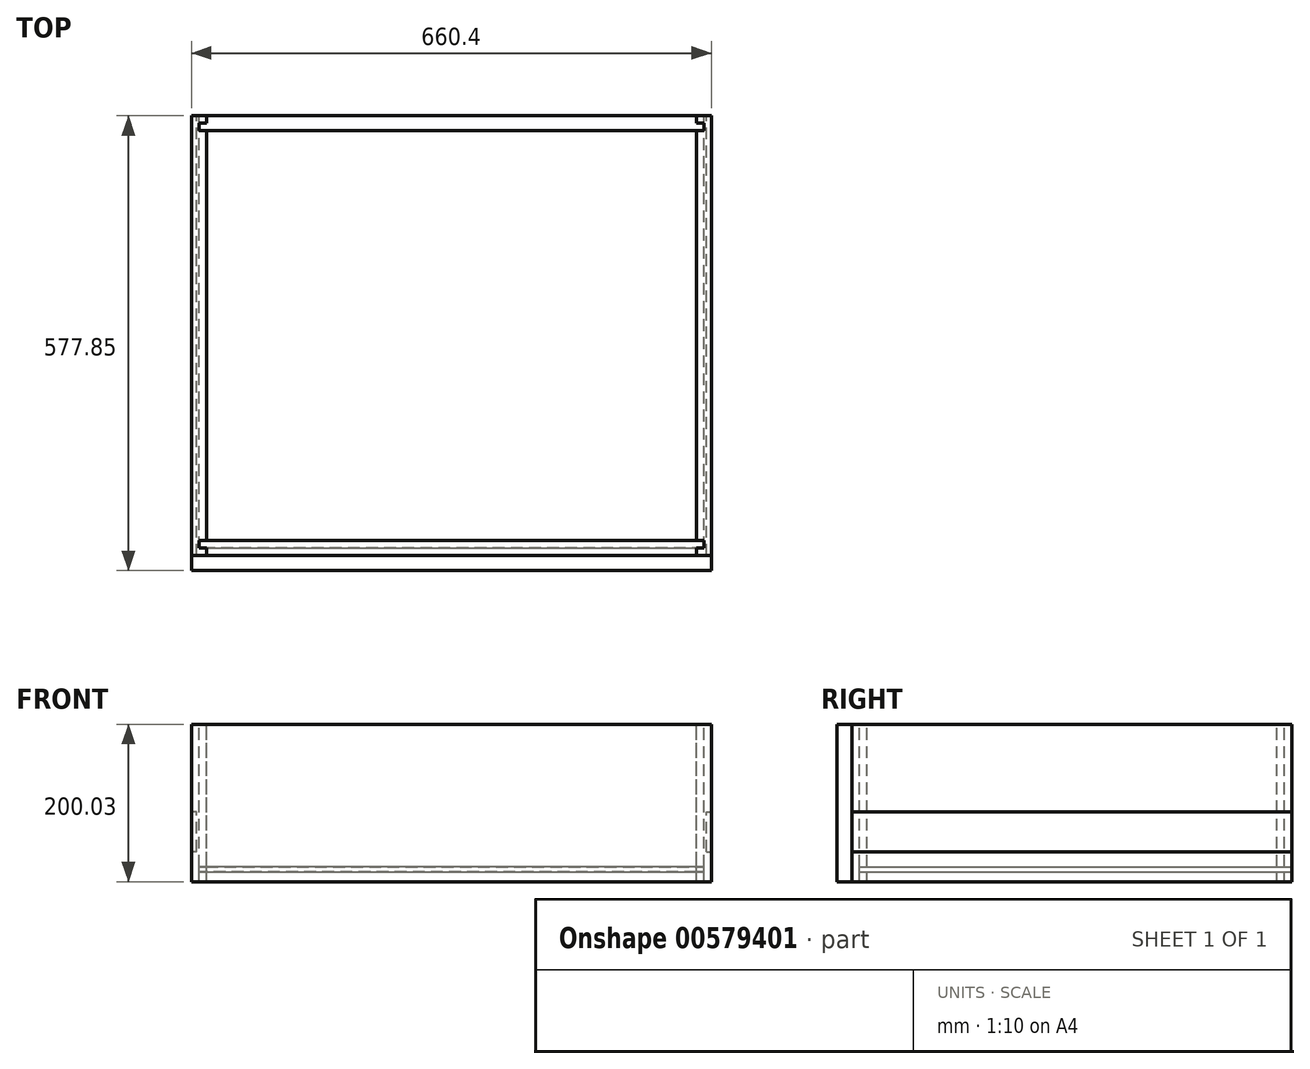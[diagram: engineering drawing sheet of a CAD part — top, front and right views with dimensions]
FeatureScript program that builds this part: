
annotation { "Feature Type Name" : "Feature", "Feature Type Description" : "" }
export const myFeature = defineFeature(function(context is Context, id is Id, definition is map)
    precondition{}
    {
        {
            var Q0;
            Q0=qCreatedBy(makeId("Top.planeOp"),FACE);
            var sketch = newSketch(context, id + "F0", { "sketchPlane" : qUnion([Q0])});
            skLineSegment(sketch, "E0.top", {"start": v(-311.15, -279.4) * mm, "end": v(311.15, -279.4) * mm});
            skPoint(sketch, "E0.middle", {"position": v(0, 0) * mm});
            skLineSegment(sketch, "E1.0", {"start": v(-320.68, -260.35) * mm, "end": v(320.68, -260.35) * mm});
            skLineSegment(sketch, "E2.0", {"start": v(-320.68, -269.88) * mm, "end": v(-311.15, -269.88) * mm});
            skLineSegment(sketch, "E3.0", {"start": v(-320.68, -260.35) * mm, "end": v(-320.68, -269.88) * mm});
            skLineSegment(sketch, "E4.0", {"start": v(320.68, -260.35) * mm, "end": v(320.68, -269.88) * mm});
            skLineSegment(sketch, "E5.0", {"start": v(311.15, -269.88) * mm, "end": v(311.15, -279.4) * mm});
            skLineSegment(sketch, "E6.trimOffspring", {"start": v(-311.15, -269.88) * mm, "end": v(-311.15, -279.4) * mm});
            skPoint(sketch, "E7.orphan", {"position": v(-330.2, -279.4) * mm});
            skLineSegment(sketch, "E8.trimOffspring", {"start": v(311.15, -269.88) * mm, "end": v(320.68, -269.88) * mm});
            skPoint(sketch, "E0.right.end.orphan", {"position": v(330.2, -279.4) * mm});
            skPoint(sketch, "E0.bottom.end.orphan", {"position": v(330.2, 279.4) * mm});
            skPoint(sketch, "E0.bottom.start.orphan", {"position": v(-330.2, 279.4) * mm});
            skSolve(sketch);
        }
        {
            var Q0;
            Q0 = qSketchRegion(id + "F0", true);
            extrude(context, id + "F1", {"entities" : qUnion([Q0]), "oppositeDirection" : true, "depth" : 200.02 * mm, "offsetDistance" : 25.4 * mm});
        }
        {
            var Q0;
            Q0=makeQuery(id+"F1.opExtrude","SWEPT_BODY",BODY,{"disambiguationData":[OSD([sQuery(id+"F0.wireOp",EDGE,"E0.top"),sQuery(id+"F0.wireOp",EDGE,"E1.0"),sQuery(id+"F0.wireOp",EDGE,"E2.0"),sQuery(id+"F0.wireOp",EDGE,"E3.0"),sQuery(id+"F0.wireOp",EDGE,"E4.0"),sQuery(id+"F0.wireOp",EDGE,"E5.0"),sQuery(id+"F0.wireOp",EDGE,"E6.trimOffspring"),sQuery(id+"F0.wireOp",EDGE,"E8.trimOffspring")])]});
            var Q1;
            Q1=qCreatedBy(makeId("Front.planeOp"),FACE);
            mirror(context, id + "F2", {"entities" : qUnion([Q0]), "mirrorPlane" : qUnion([Q1])});
        }
        {
            var Q0;
            Q0=qCreatedBy(makeId("Top.planeOp"),FACE);
            var sketch = newSketch(context, id + "F3", { "sketchPlane" : qUnion([Q0])});
            skLineSegment(sketch, "E9.0", {"start": v(-320.68, 260.35) * mm, "end": v(-320.68, 269.88) * mm});
            skLineSegment(sketch, "E10.0", {"start": v(-320.68, -260.35) * mm, "end": v(-320.68, -269.88) * mm});
            skLineSegment(sketch, "E11.0", {"start": v(-311.15, -269.88) * mm, "end": v(-311.15, -279.4) * mm});
            skLineSegment(sketch, "E12.0", {"start": v(-320.68, -260.35) * mm, "end": v(320.68, -260.35) * mm});
            skPoint(sketch, "E13.orphan", {"position": v(-311.15, 269.88) * mm});
            skLineSegment(sketch, "E14.0", {"start": v(-330.2, -279.4) * mm, "end": v(-330.2, 279.4) * mm});
            skLineSegment(sketch, "E15.0", {"start": v(-330.2, 279.4) * mm, "end": v(-311.15, 279.4) * mm});
            skLineSegment(sketch, "E16.0", {"start": v(-330.2, -279.4) * mm, "end": v(-311.15, -279.4) * mm});
            skPoint(sketch, "E17.orphan", {"position": v(311.15, 279.4) * mm});
            skLineSegment(sketch, "E18.0", {"start": v(-311.15, -260.35) * mm, "end": v(-311.15, 260.35) * mm});
            skLineSegment(sketch, "E19.0", {"start": v(-320.68, 269.88) * mm, "end": v(-311.15, 269.88) * mm});
            skLineSegment(sketch, "E20.0", {"start": v(-320.68, 260.35) * mm, "end": v(-311.15, 260.35) * mm});
            skLineSegment(sketch, "E21.0", {"start": v(-311.15, 269.88) * mm, "end": v(-311.15, 279.4) * mm});
            skLineSegment(sketch, "E22.0.0", {"start": v(-311.15, -260.35) * mm, "end": v(-320.68, -260.35) * mm});
            skLineSegment(sketch, "E22.0.2", {"start": v(-320.68, -269.88) * mm, "end": v(-311.15, -269.88) * mm});
            skLineSegment(sketch, "E22.0.4", {"start": v(-311.15, -279.4) * mm, "end": v(311.15, -279.4) * mm});
            skLineSegment(sketch, "E22.0.5", {"start": v(311.15, -279.4) * mm, "end": v(311.15, -269.88) * mm});
            skLineSegment(sketch, "E22.0.6", {"start": v(311.15, -269.88) * mm, "end": v(320.68, -269.88) * mm});
            skLineSegment(sketch, "E22.0.7", {"start": v(320.68, -269.88) * mm, "end": v(320.68, -260.35) * mm});
            skPoint(sketch, "E23.orphan", {"position": v(320.68, 260.35) * mm});
            skSolve(sketch);
        }
        {
            var Q0;
            Q0 = qSketchRegion(id + "F3", true);
            extrude(context, id + "F4", {"entities" : qUnion([Q0]), "oppositeDirection" : true, "depth" : 200.02 * mm, "offsetDistance" : 25.4 * mm});
        }
        {
            var Q0;
            Q0=makeQuery(id+"F4.opExtrude","SWEPT_BODY",BODY,{"disambiguationData":[OSD([sQuery(id+"F3.wireOp",EDGE,"E9.0"),sQuery(id+"F3.wireOp",EDGE,"E12.0"),sQuery(id+"F3.wireOp",EDGE,"E14.0"),sQuery(id+"F3.wireOp",EDGE,"E15.0"),sQuery(id+"F3.wireOp",EDGE,"E16.0"),sQuery(id+"F3.wireOp",EDGE,"E18.0"),sQuery(id+"F3.wireOp",EDGE,"E19.0"),sQuery(id+"F3.wireOp",EDGE,"E20.0"),sQuery(id+"F3.wireOp",EDGE,"E21.0"),sQuery(id+"F3.wireOp",EDGE,"E22.0.4"),sQuery(id+"F3.wireOp",EDGE,"E22.0.5"),sQuery(id+"F3.wireOp",EDGE,"E22.0.6"),sQuery(id+"F3.wireOp",EDGE,"E22.0.7")])]});
            var Q1;
            Q1=qCreatedBy(makeId("Right.planeOp"),FACE);
            mirror(context, id + "F5", {"entities" : qUnion([Q0]), "mirrorPlane" : qUnion([Q1])});
        }
        {
            var Q0;
            Q0=makeQuery(id+"F2.opPattern","COPY",FACE,{"derivedFrom":makeQuery(id+"F1.opExtrude","SWEPT_FACE",FACE,{"disambiguationData":[OSD([sQuery(id+"F0.wireOp",EDGE,"E0.top")])]}),"instanceName":"1"});
            var sketch = newSketch(context, id + "F6", { "sketchPlane" : qUnion([Q0])});
            skLineSegment(sketch, "E24.0", {"start": v(320.68, -180.97) * mm, "end": v(-320.68, -180.97) * mm});
            skPoint(sketch, "E25.orphan", {"position": v(-311.15, -200.03) * mm});
            skPoint(sketch, "E26.0.end.orphan", {"position": v(-311.15, 0) * mm});
            skLineSegment(sketch, "E27.0", {"start": v(-320.68, -187.33) * mm, "end": v(-320.68, -180.97) * mm});
            skLineSegment(sketch, "E28.0", {"start": v(320.68, -187.33) * mm, "end": v(320.68, -180.97) * mm});
            skLineSegment(sketch, "E29.0", {"start": v(320.68, -187.33) * mm, "end": v(-320.68, -187.33) * mm});
            skPoint(sketch, "E30.orphan", {"position": v(310.51, -180.97) * mm});
            skPoint(sketch, "E31.orphan", {"position": v(-311.79, -180.97) * mm});
            skSolve(sketch);
        }
        {
            var Q0;
            Q0 = qSketchRegion(id + "F6", true);
            extrude(context, id + "F7", {"entities" : qUnion([Q0]), "operationType" : NewBodyOperationType.REMOVE, "oppositeDirection" : true, "depth" : 549.27 * mm, "offsetDistance" : 25.4 * mm});
        }
        {
            var Q0;
            {var subQ2=sQuery(id+"F0.wireOp",EDGE,"E0.top");Q0=makeQuery(id+"F7.boolean.opBoolean","SPLIT",FACE,{"disambiguationData":[TD([makeQuery(id+"F7.opExtrude","SWEPT_FACE",FACE,{"disambiguationData":[OSD([sQuery(id+"F6.wireOp",EDGE,"E24.0")])]})])],"derivedFrom":makeQuery(id+"F2.opPattern","COPY",FACE,{"derivedFrom":makeQuery(id+"F1.opExtrude","SWEPT_FACE",FACE,{"disambiguationData":[OSD([subQ2])]}),"instanceName":"1"})});}
            var sketch = newSketch(context, id + "F8", { "sketchPlane" : qUnion([Q0])});
            skLineSegment(sketch, "E32.0", {"start": v(-320.68, -187.33) * mm, "end": v(-320.68, -180.97) * mm});
            skLineSegment(sketch, "E33.0", {"start": v(-311.15, -180.97) * mm, "end": v(-320.68, -180.97) * mm});
            skLineSegment(sketch, "E34.0", {"start": v(311.15, -180.97) * mm, "end": v(-311.15, -180.97) * mm});
            skLineSegment(sketch, "E35.0", {"start": v(-311.15, -187.33) * mm, "end": v(-320.68, -187.33) * mm});
            skLineSegment(sketch, "E36.0", {"start": v(311.15, -187.33) * mm, "end": v(-311.15, -187.33) * mm});
            skLineSegment(sketch, "E37.0", {"start": v(320.68, -180.97) * mm, "end": v(311.15, -180.97) * mm});
            skLineSegment(sketch, "E38.0", {"start": v(320.68, -187.33) * mm, "end": v(311.15, -187.33) * mm});
            skLineSegment(sketch, "E39.0", {"start": v(320.68, -187.33) * mm, "end": v(320.68, -180.97) * mm});
            skSolve(sketch);
        }
        {
            var Q0;
            Q0 = qSketchRegion(id + "F8", true);
            var Q1;
            {var subQ0=sQuery(id+"F6.wireOp",EDGE,"E27.0");var subQ1=sQuery(id+"F6.wireOp",EDGE,"E24.0");var subQ2=sQuery(id+"F6.wireOp",EDGE,"E29.0");Q1=makeQuery(id+"F7.boolean.opBoolean","COPY",FACE,{"disambiguationData":[TD([makeQuery(id+"F5.opPattern","COPY",FACE,{"derivedFrom":makeQuery(id+"F4.opExtrude","SWEPT_FACE",FACE,{"disambiguationData":[OSD([sQuery(id+"F3.wireOp",EDGE,"E22.0.5")])]}),"instanceName":"1"})])],"derivedFrom":makeQuery(id+"F7.opExtrude","CAP_FACE",FACE,{"disambiguationData":[OSD([subQ1,subQ0,sQuery(id+"F6.wireOp",EDGE,"E28.0"),subQ2])],"isStart":false})});}
            extrude(context, id + "F9", {"entities" : qUnion([Q0]), "endBound" : BoundingType.UP_TO_SURFACE, "oppositeDirection" : true, "depth" : 25.4 * mm, "endBoundEntityFace" : qUnion([Q1]), "offsetDistance" : 25.4 * mm});
        }
        {
            var Q0;
            Q0=makeQuery(id+"F4.opExtrude","SWEPT_FACE",FACE,{"disambiguationData":[OSD([sQuery(id+"F3.wireOp",EDGE,"E16.0"),sQuery(id+"F3.wireOp",EDGE,"E22.0.4")])]});
            var sketch = newSketch(context, id + "F10", { "sketchPlane" : qUnion([Q0])});
            skLineSegment(sketch, "E40.0", {"start": v(-330.2, -200.03) * mm, "end": v(-330.2, 0) * mm});
            skLineSegment(sketch, "E41.0", {"start": v(-311.15, 0) * mm, "end": v(311.15, 0) * mm});
            skLineSegment(sketch, "E42.0", {"start": v(-330.2, 0) * mm, "end": v(311.15, 0) * mm});
            skLineSegment(sketch, "E43.0", {"start": v(330.2, 0) * mm, "end": v(-311.15, 0) * mm});
            skLineSegment(sketch, "E44.0", {"start": v(330.2, -200.03) * mm, "end": v(330.2, 0) * mm});
            skLineSegment(sketch, "E45.0", {"start": v(330.2, -200.03) * mm, "end": v(-311.15, -200.03) * mm});
            skLineSegment(sketch, "E46.0", {"start": v(-330.2, -200.03) * mm, "end": v(311.15, -200.03) * mm});
            skSolve(sketch);
        }
        {
            var Q0;
            Q0 = qSketchRegion(id + "F10", true);
            extrude(context, id + "F11", {"entities" : qUnion([Q0]), "depth" : 19.05 * mm, "offsetDistance" : 25.4 * mm});
        }
        {
            var Q0;
            Q0=makeQuery(id+"F5.opPattern","COPY",FACE,{"derivedFrom":makeQuery(id+"F4.opExtrude","SWEPT_FACE",FACE,{"disambiguationData":[OSD([sQuery(id+"F3.wireOp",EDGE,"E14.0")])]}),"instanceName":"1"});
            var sketch = newSketch(context, id + "F12", { "sketchPlane" : qUnion([Q0])});
            skLineSegment(sketch, "E47.0", {"start": v(-279.4, -161.93) * mm, "end": v(-279.4, -111.12) * mm});
            skLineSegment(sketch, "E48.0", {"start": v(279.4, -161.93) * mm, "end": v(279.4, -111.12) * mm});
            skLineSegment(sketch, "E49.0", {"start": v(-279.4, -161.93) * mm, "end": v(279.4, -161.93) * mm});
            skLineSegment(sketch, "E50.0", {"start": v(-279.4, -111.12) * mm, "end": v(279.4, -111.12) * mm});
            skPoint(sketch, "E51.orphan", {"position": v(-279.4, 0) * mm});
            skPoint(sketch, "E52.orphan", {"position": v(-279.4, -200.03) * mm});
            skPoint(sketch, "E53.orphan", {"position": v(279.4, 0) * mm});
            skPoint(sketch, "E54.orphan", {"position": v(279.4, -200.03) * mm});
            skSolve(sketch);
        }
        {
            var Q0;
            Q0 = qSketchRegion(id + "F12", true);
            extrude(context, id + "F13", {"entities" : qUnion([Q0]), "operationType" : NewBodyOperationType.REMOVE, "oppositeDirection" : true, "depth" : 6.35 * mm, "offsetDistance" : 25.4 * mm});
        }
        {
            var Q0;
            Q0=makeQuery(id+"F4.opExtrude","SWEPT_FACE",FACE,{"disambiguationData":[OSD([sQuery(id+"F3.wireOp",EDGE,"E14.0")])]});
            var sketch = newSketch(context, id + "F14", { "sketchPlane" : qUnion([Q0])});
            skLineSegment(sketch, "E55.0", {"start": v(-279.4, -161.93) * mm, "end": v(-279.4, -111.12) * mm});
            skLineSegment(sketch, "E56.0", {"start": v(279.4, -161.93) * mm, "end": v(279.4, -111.12) * mm});
            skLineSegment(sketch, "E57.0", {"start": v(279.4, -161.93) * mm, "end": v(-279.4, -161.93) * mm});
            skLineSegment(sketch, "E58.0", {"start": v(279.4, -111.12) * mm, "end": v(-279.4, -111.12) * mm});
            skPoint(sketch, "E59.orphan", {"position": v(-279.4, 0) * mm});
            skPoint(sketch, "E60.orphan", {"position": v(-279.4, -200.03) * mm});
            skPoint(sketch, "E61.orphan", {"position": v(279.4, -200.03) * mm});
            skPoint(sketch, "E62.orphan", {"position": v(279.4, 0) * mm});
            skSolve(sketch);
        }
        {
            var Q0;
            Q0 = qSketchRegion(id + "F14", true);
            extrude(context, id + "F15", {"entities" : qUnion([Q0]), "operationType" : NewBodyOperationType.REMOVE, "oppositeDirection" : true, "depth" : 6.35 * mm, "offsetDistance" : 25.4 * mm});
        }
    });
